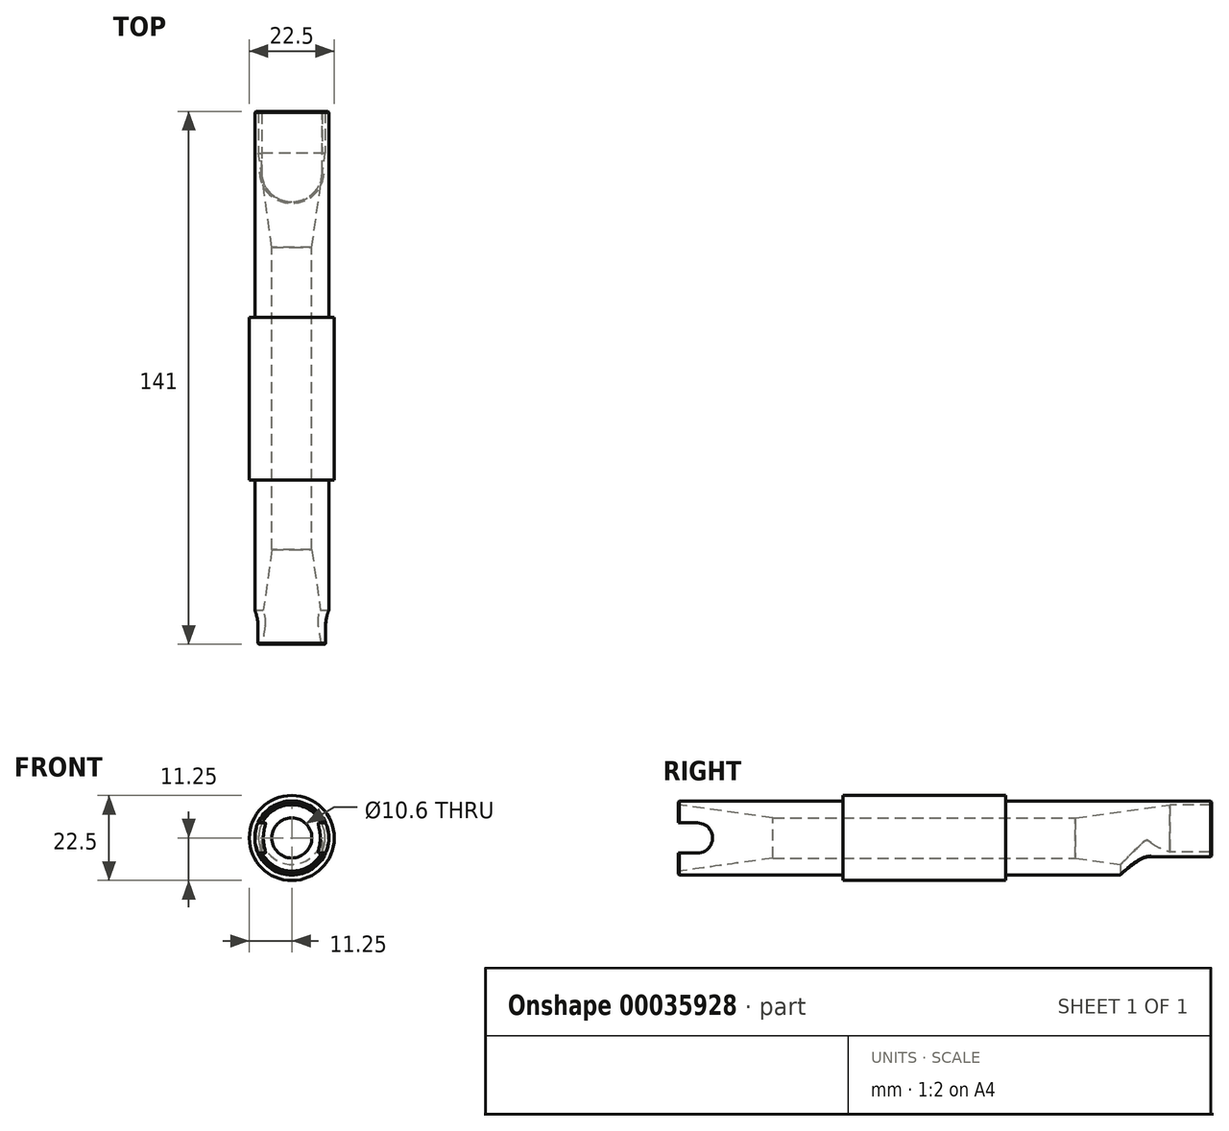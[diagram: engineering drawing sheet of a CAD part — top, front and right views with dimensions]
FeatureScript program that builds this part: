
annotation { "Feature Type Name" : "Feature", "Feature Type Description" : "" }
export const myFeature = defineFeature(function(context is Context, id is Id, definition is map)
    precondition{}
    {
        {
            var Q0;
            Q0=qCreatedBy(makeId("Front.planeOp"),FACE);
            var sketch = newSketch(context, id + "F0", { "sketchPlane" : qUnion([Q0])});
            skCircle(sketch, "E0", {"center": v(0, 0) * mm, "radius": 9.8 * mm});
            skCircle(sketch, "E1", {"center": v(0, 0) * mm, "radius": 11.25 * mm});
            skCircle(sketch, "E2", {"center": v(0, 0) * mm, "radius": 5.3 * mm});
            skSolve(sketch);
        }
        {
            var Q0;
            Q0=makeQuery(id+"F0.imprint","IMPRINT",FACE,{"disambiguationData":[TD([[makeQuery(id+"F0.imprint","IMPRINT",EDGE,{"derivedFrom":sQuery(id+"F0.wireOp",EDGE,"E0")}),-1.0]])]});
            extrude(context, id + "F1", {"entities" : qUnion([Q0]), "endBound" : BoundingType.SYMMETRIC, "depth" : 43 * mm});
        }
        {
            var Q0;
            Q0=makeQuery(id+"F0.imprint","IMPRINT",FACE,{"disambiguationData":[TD([[makeQuery(id+"F0.imprint","IMPRINT",EDGE,{"derivedFrom":sQuery(id+"F0.wireOp",EDGE,"E0")}),1.0]])]});
            extrude(context, id + "F2", {"entities" : qUnion([Q0]), "operationType" : NewBodyOperationType.ADD, "endBound" : BoundingType.SYMMETRIC, "depth" : 130 * mm});
        }
        {
            var Q0;
            Q0=makeQuery(id+"F2.opExtrude","CAP_EDGE",EDGE,{"disambiguationData":[OSD([sQuery(id+"F0.wireOp",EDGE,"E2")])],"isStart":false});
            chamfer(context, id + "F3", {"entities" : qUnion([Q0]), "chamferType" : ChamferType.TWO_OFFSETS, "width1" : 25 * mm, "oppositeDirection" : false, "width2" : 3.5 * mm, "tangentPropagation" : true});
        }
        {
            var Q0;
            Q0=makeQuery(id+"F2.opExtrude","CAP_EDGE",EDGE,{"disambiguationData":[OSD([sQuery(id+"F0.wireOp",EDGE,"E2")])],"isStart":true});
            chamfer(context, id + "F4", {"entities" : qUnion([Q0]), "chamferType" : ChamferType.TWO_OFFSETS, "width1" : 3.5 * mm, "oppositeDirection" : false, "width2" : 25 * mm, "tangentPropagation" : true});
        }
        {
            var Q0;
            Q0=qCreatedBy(makeId("Top.planeOp"),FACE);
            var sketch = newSketch(context, id + "F5", { "sketchPlane" : qUnion([Q0])});
            skCircle(sketch, "E3", {"center": v(0, 60) * mm, "radius": 8 * mm});
            skLineSegment(sketch, "E4", {"start": v(0, 0) * mm, "end": v(0, 60) * mm});
            skLineSegment(sketch, "E5.bottom", {"start": v(-8, 60) * mm, "end": v(0, 60) * mm});
            skLineSegment(sketch, "E5.top", {"start": v(-8, 96.12) * mm, "end": v(0, 96.12) * mm});
            skLineSegment(sketch, "E5.left", {"start": v(-8, 60) * mm, "end": v(-8, 96.12) * mm});
            skLineSegment(sketch, "E5.right", {"start": v(0, 60) * mm, "end": v(0, 96.12) * mm});
            skLineSegment(sketch, "E6.bottom", {"start": v(8, 60) * mm, "end": v(0, 60) * mm});
            skLineSegment(sketch, "E6.top", {"start": v(8, 96.12) * mm, "end": v(0, 96.12) * mm});
            skLineSegment(sketch, "E6.left", {"start": v(8, 60) * mm, "end": v(8, 96.12) * mm});
            skSolve(sketch);
        }
        {
            var Q0;
            Q0=makeQuery(id+"F2.opExtrude","CAP_FACE",FACE,{"disambiguationData":[OSD([sQuery(id+"F0.wireOp",EDGE,"E0"),sQuery(id+"F0.wireOp",EDGE,"E2")])],"isStart":true});
            extrude(context, id + "F6", {"entities" : qUnion([Q0]), "operationType" : NewBodyOperationType.ADD, "depth" : 11 * mm});
        }
        {
            var Q0;
            {var subQ0=sQuery(id+"F5.wireOp",EDGE,"E6.top");Q0=makeQuery(id+"F5.imprint","IMPRINT",FACE,{"disambiguationData":[TD([[makeQuery(id+"F5.imprint","IMPRINT",EDGE,{"derivedFrom":subQ0}),1.0]])]});}
            var Q1;
            {var subQ3=sQuery(id+"F5.wireOp",EDGE,"E5.top");Q1=makeQuery(id+"F5.imprint","IMPRINT",FACE,{"disambiguationData":[TD([[makeQuery(id+"F5.imprint","IMPRINT",EDGE,{"derivedFrom":subQ3}),-1.0]])]});}
            var Q2;
            {var subQ3=sQuery(id+"F5.wireOp",EDGE,"E6.bottom");Q2=makeQuery(id+"F5.imprint","IMPRINT",FACE,{"disambiguationData":[TD([[makeQuery(id+"F5.imprint","IMPRINT",EDGE,{"derivedFrom":subQ3}),-1.0]])]});}
            var Q3;
            {var subQ3=sQuery(id+"F5.wireOp",EDGE,"E5.bottom");Q3=makeQuery(id+"F5.imprint","IMPRINT",FACE,{"disambiguationData":[TD([[makeQuery(id+"F5.imprint","IMPRINT",EDGE,{"derivedFrom":subQ3}),1.0]])]});}
            var Q4;
            {var subQ0=sQuery(id+"F5.wireOp",EDGE,"E6.bottom");Q4=makeQuery(id+"F5.imprint","IMPRINT",FACE,{"disambiguationData":[TD([[makeQuery(id+"F5.imprint","IMPRINT",EDGE,{"derivedFrom":subQ0}),1.0]])]});}
            var Q5;
            {var subQ0=sQuery(id+"F5.wireOp",EDGE,"E5.bottom");Q5=makeQuery(id+"F5.imprint","IMPRINT",FACE,{"disambiguationData":[TD([[makeQuery(id+"F5.imprint","IMPRINT",EDGE,{"derivedFrom":subQ0}),-1.0]])]});}
            extrude(context, id + "F7", {"entities" : qUnion([Q0, Q1, Q2, Q3, Q4, Q5]), "operationType" : NewBodyOperationType.REMOVE, "oppositeDirection" : true, "depth" : 25 * mm});
        }
        {
            var Q0;
            {var subQ0=sQuery(id+"F0.wireOp",EDGE,"E0");Q0=makeQuery(id+"F7.boolean.opBoolean","INTERSECT",EDGE,{"derivedFrom":[makeQuery(id+"F6.boolean.opBoolean","MERGE",FACE,{"derivedFrom":[makeQuery(id+"F2.boolean.opBoolean","SPLIT",FACE,{"disambiguationData":[TD([makeQuery(id+"F1.opExtrude","CAP_FACE",FACE,{"disambiguationData":[OSD([subQ0,sQuery(id+"F0.wireOp",EDGE,"E1")])],"isStart":true})])],"derivedFrom":makeQuery(id+"F2.opExtrude","SWEPT_FACE",FACE,{"disambiguationData":[OSD([subQ0])]})}),makeQuery(id+"F6.opExtrude","SWEPT_FACE",FACE,{"disambiguationData":[OSD([subQ0])]})]}),makeQuery(id+"F7.opExtrude","SWEPT_FACE",FACE,{"disambiguationData":[OSD([sQuery(id+"F5.wireOp",EDGE,"E3")])]})]});}
            fillet(context, id + "F8", {"entities" : qUnion([Q0]), "radius" : .3 * mm, "tangentPropagation" : true, "allowEdgeOverflow" : false});
        }
        {
            var Q0;
            Q0=makeQuery(id+"F6.opExtrude","CAP_EDGE",EDGE,{"disambiguationData":[OSD([sQuery(id+"F0.wireOp",EDGE,"E0")])],"isStart":false});
            var Q1;
            Q1=makeQuery(id+"F2.opExtrude","CAP_EDGE",EDGE,{"disambiguationData":[OSD([sQuery(id+"F0.wireOp",EDGE,"E0")])],"isStart":false});
            chamfer(context, id + "F9", {"entities" : qUnion([Q0, Q1]), "width" : .25 * mm, "tangentPropagation" : true});
        }
        {
            var Q0;
            Q0=makeQuery(id+"F1.opExtrude","CAP_EDGE",EDGE,{"disambiguationData":[OSD([sQuery(id+"F0.wireOp",EDGE,"E0")])],"isStart":false});
            var Q1;
            Q1=makeQuery(id+"F1.opExtrude","CAP_EDGE",EDGE,{"disambiguationData":[OSD([sQuery(id+"F0.wireOp",EDGE,"E0")])],"isStart":true});
            fillet(context, id + "F10", {"entities" : qUnion([Q0, Q1]), "radius" : .25 * mm, "tangentPropagation" : true, "allowEdgeOverflow" : false});
        }
        {
            var Q0;
            Q0=qCreatedBy(makeId("Right.planeOp"),FACE);
            var sketch = newSketch(context, id + "F11", { "sketchPlane" : qUnion([Q0])});
            skLineSegment(sketch, "E7.rect.bottom", {"start": v(-56, -4) * mm, "end": v(-74, -4) * mm});
            skLineSegment(sketch, "E7.rect.top", {"start": v(-56, 4) * mm, "end": v(-74, 4) * mm});
            skLineSegment(sketch, "E7.rect.left", {"start": v(-56, -4) * mm, "end": v(-56, 4) * mm});
            skLineSegment(sketch, "E7.rect.right", {"start": v(-74, -4) * mm, "end": v(-74, 4) * mm});
            skPoint(sketch, "E7.rect.middle", {"position": v(-65, 0) * mm});
            skCircle(sketch, "E8", {"center": v(-60, 0) * mm, "radius": 4 * mm});
            skSolve(sketch);
        }
        {
            var Q0;
            {var subQ0=sQuery(id+"F11.wireOp",EDGE,"E7.rect.right");Q0=makeQuery(id+"F11.imprint","IMPRINT",FACE,{"disambiguationData":[TD([[makeQuery(id+"F11.imprint","IMPRINT",EDGE,{"derivedFrom":subQ0}),-1.0]])]});}
            var Q1;
            {var subQ0=sQuery(id+"F11.wireOp",EDGE,"E8");var subQ1=makeQuery(id+"F11.imprint","INTERSECT",VERTEX,{"derivedFrom":[sQuery(id+"F11.wireOp",EDGE,"E7.rect.top"),subQ0]});Q1=makeQuery(id+"F11.imprint","IMPRINT",FACE,{"disambiguationData":[TD([[makeQuery(id+"F11.imprint","IMPRINT",EDGE,{"disambiguationData":[TD([[subQ1,1.0]])],"derivedFrom":subQ0}),1.0]])]});}
            extrude(context, id + "F12", {"entities" : qUnion([Q0, Q1]), "operationType" : NewBodyOperationType.REMOVE, "endBound" : BoundingType.SYMMETRIC, "oppositeDirection" : true, "depth" : 50 * mm});
        }
    });
